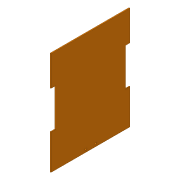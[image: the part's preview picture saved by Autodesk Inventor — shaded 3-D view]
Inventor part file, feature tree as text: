
AUTODESK INVENTOR PART (.ipt)
format: ipt  version: 2016 (Build 200138000, 138)  size: 144,384 bytes
history: native  units: in
note: dims shown in document units (in); Inventor stores cm internally (conversion verified against a paired STEP export)
features: extrude x3, sketch x3, fillet x2, mirror x1, plane x1
ambient origin geometry x8: Origin, YZ Plane, XZ Plane, XY Plane, X Axis, Y Axis, Z Axis, Center Point
bodies: Solid1 (feature_tree)
feature tree (10):
  extrude  "Extrusion1"  Depth=8.9in
  extrude  "Extrusion2"  Depth=4.25in
  mirror  "Mirror1"
  plane  "Work Plane1"
  fillet  "Fillet2"  [1 undecoded]
  fillet  "Fillet4"  [1 undecoded]
  extrude  "Extrusion4"  Depth=3.4in
  sketch  "Sketch1"  dims[d0=11.6in d1=8.9in]
  sketch  "Sketch2"  dims[d2=0.1125in d3=0.0in d4=4.25in d5=0.0in d6=0.0in]
  sketch  "Sketch7"  dims[d7=0.5in d8=3.4in d9=0.1125in d10=0.0in d11=0.25in d19=0.03in d21=0.01in d22=0.2in d23=0.55in d24=0.3in d27=1.0in d28=0.0in]
note: 2 required parameter values undecoded (feature->parameter linkage not recoverable at this tier; creation-order binding heuristic only, values carry confidence <= 0.55)
